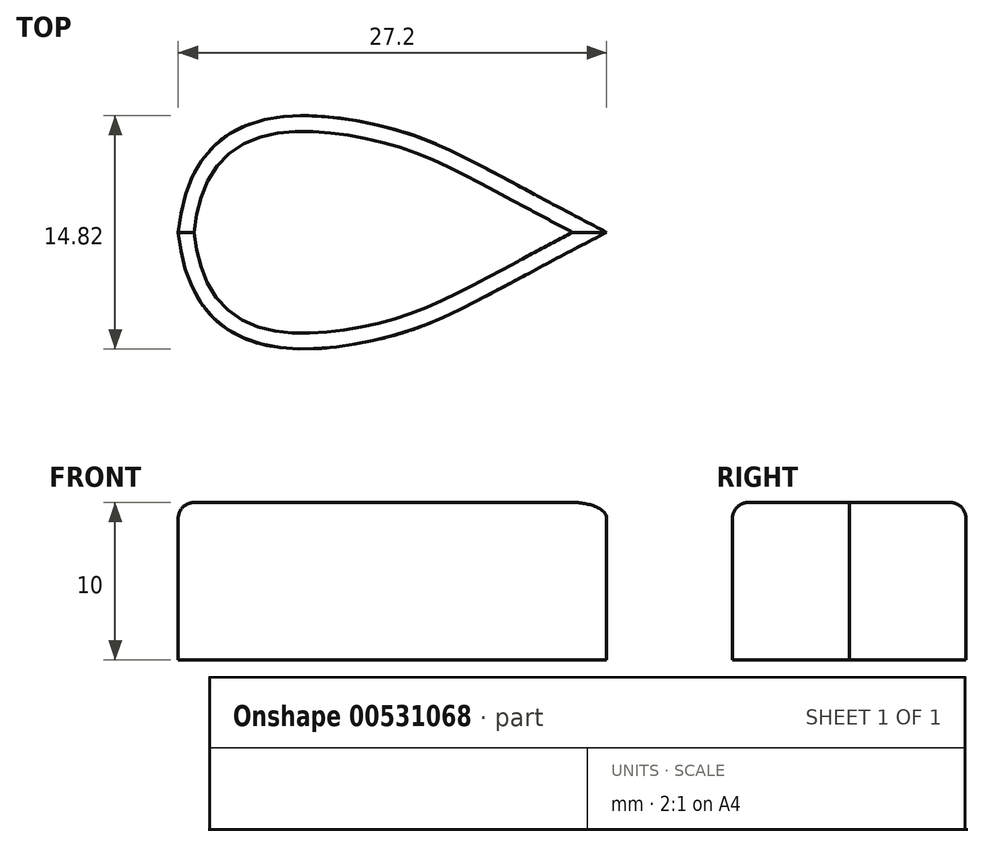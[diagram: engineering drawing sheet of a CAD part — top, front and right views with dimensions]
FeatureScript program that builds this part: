
annotation { "Feature Type Name" : "Feature", "Feature Type Description" : "" }
export const myFeature = defineFeature(function(context is Context, id is Id, definition is map)
    precondition{}
    {
        {
            var Q0;
            Q0=qCreatedBy(makeId("Top.planeOp"),FACE);
            var sketch = newSketch(context, id + "F0", { "sketchPlane" : qUnion([Q0])});
            skFitSpline(sketch, "E0", {"points": [v(-14.96, 0) * mm, v(-3.22, 7) * mm, v(12.24, 0) * mm], "startDerivative": vector(5.04, 52.08) * mm, "endDerivative": vector(51.03, -26.4) * mm});
            skFitSpline(sketch, "E1.MirrorCS", {"points": [v(-14.96, 0) * mm, v(-3.22, -7) * mm, v(12.24, 0) * mm], "startDerivative": vector(5.04, -52.08) * mm, "endDerivative": vector(51.03, 26.4) * mm});
            skLineSegment(sketch, "E2", {"start": v(7.66, 2.41) * mm, "end": v(18.38, 5.47) * mm});
            skLineSegment(sketch, "E3", {"start": v(18.38, 5.47) * mm, "end": v(18.38, -6.28) * mm});
            skLineSegment(sketch, "E4", {"start": v(18.38, -6.28) * mm, "end": v(7.08, -2.73) * mm});
            skSolve(sketch);
        }
        {
            var Q0;
            Q0=makeQuery(id+"F0.imprint","IMPRINT",FACE,{"disambiguationData":[TD([[makeQuery(id+"F0.imprint","IMPRINT",EDGE,{"derivedFrom":sQuery(id+"F0.wireOp",EDGE,"E0")}),-1.0]])]});
            extrude(context, id + "F1", {"entities" : qUnion([Q0]), "depth" : 10 * mm, "offsetDistance" : 25 * mm});
        }
        {
            var Q0;
            Q0=makeQuery(id+"F1.opExtrude","CAP_FACE",FACE,{"disambiguationData":[OSD([sQuery(id+"F0.wireOp",EDGE,"E0"),sQuery(id+"F0.wireOp",EDGE,"E1.MirrorCS"),sQuery(id+"F0.wireOp",EDGE,"E2"),sQuery(id+"F0.wireOp",EDGE,"E3"),sQuery(id+"F0.wireOp",EDGE,"E4")])],"isStart":false});
            fillet(context, id + "F2", {"entities" : qUnion([Q0]), "radius" : 1 * mm, "tangentPropagation" : true, "allowEdgeOverflow" : false});
        }
    });
